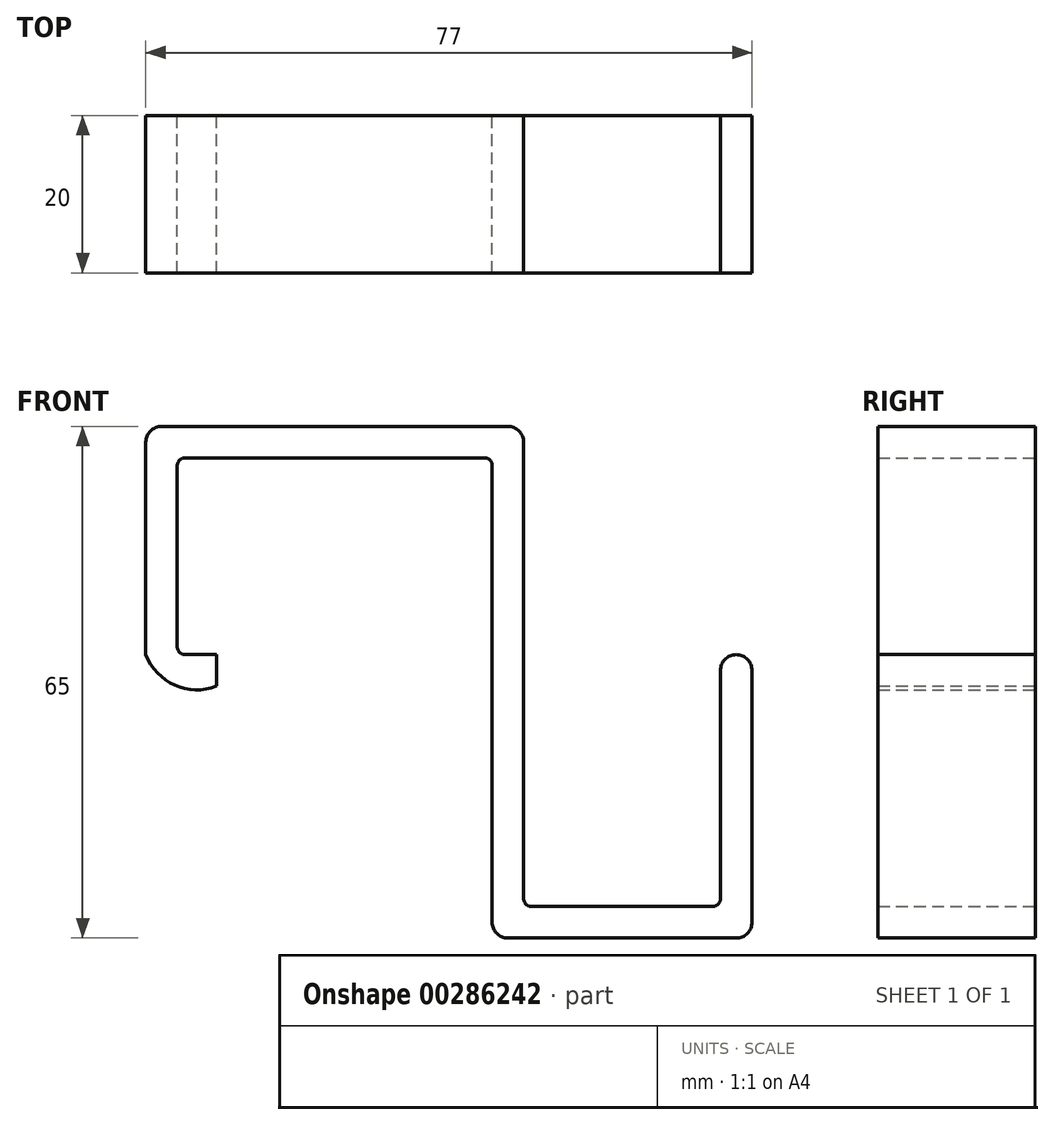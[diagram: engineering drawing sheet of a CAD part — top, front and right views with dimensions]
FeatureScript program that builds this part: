
annotation { "Feature Type Name" : "Feature", "Feature Type Description" : "" }
export const myFeature = defineFeature(function(context is Context, id is Id, definition is map)
    precondition{}
    {
        {
            var Q0;
            Q0=qCreatedBy(makeId("Front.planeOp"),FACE);
            var sketch = newSketch(context, id + "F0", { "sketchPlane" : qUnion([Q0])});
            skLineSegment(sketch, "E0", {"start": v(-24, 0) * mm, "end": v(-24, 29) * mm});
            skLineSegment(sketch, "E1", {"start": v(-24, 29) * mm, "end": v(24, 29) * mm});
            skLineSegment(sketch, "E2", {"start": v(24, 29) * mm, "end": v(24, -32) * mm});
            skLineSegment(sketch, "E3", {"start": v(24, -32) * mm, "end": v(49, -32) * mm});
            skLineSegment(sketch, "E4", {"start": v(49, -32) * mm, "end": v(49, 0) * mm});
            skLineSegment(sketch, "E5", {"start": v(49, 0) * mm, "end": v(53, 0) * mm});
            skLineSegment(sketch, "E6", {"start": v(53, 0) * mm, "end": v(53, -36) * mm});
            skLineSegment(sketch, "E7", {"start": v(53, -36) * mm, "end": v(20, -36) * mm});
            skLineSegment(sketch, "E8", {"start": v(20, -36) * mm, "end": v(20, 25) * mm});
            skLineSegment(sketch, "E9", {"start": v(20, 25) * mm, "end": v(-20, 25) * mm});
            skLineSegment(sketch, "E10", {"start": v(-20, 25) * mm, "end": v(-20, 0) * mm});
            skLineSegment(sketch, "E11", {"start": v(-20, 0) * mm, "end": v(-24, 0) * mm});
            skLineSegment(sketch, "E12", {"start": v(-15, -4) * mm, "end": v(-15, 0) * mm});
            skLineSegment(sketch, "E13", {"start": v(-15, 0) * mm, "end": v(-20, 0) * mm});
            skArc(sketch, "E14", {"start": v(-24, 0) * mm, "mid": v(-20.33, -3.86) * mm, "end": v(-15, -4) * mm});
            skSolve(sketch);
        }
        {
            var Q0;
            Q0 = qSketchRegion(id + "F0", true);
            extrude(context, id + "F1", {"entities" : qUnion([Q0]), "depth" : 20 * mm});
        }
        {
            var Q0;
            Q0=makeQuery(id+"F1.opExtrude","SWEPT_EDGE",EDGE,{"disambiguationData":[OSD([sQuery(id+"F0.wireOp",EDGE,"E10"),sQuery(id+"F0.wireOp",EDGE,"E11"),sQuery(id+"F0.wireOp",EDGE,"E13")])]});
            var Q1;
            Q1=makeQuery(id+"F1.opExtrude","SWEPT_EDGE",EDGE,{"disambiguationData":[OSD([sQuery(id+"F0.wireOp",EDGE,"E9"),sQuery(id+"F0.wireOp",EDGE,"E10")])]});
            var Q2;
            Q2=makeQuery(id+"F1.opExtrude","SWEPT_EDGE",EDGE,{"disambiguationData":[OSD([sQuery(id+"F0.wireOp",EDGE,"E8"),sQuery(id+"F0.wireOp",EDGE,"E9")])]});
            var Q3;
            Q3=makeQuery(id+"F1.opExtrude","SWEPT_EDGE",EDGE,{"disambiguationData":[OSD([sQuery(id+"F0.wireOp",EDGE,"E2"),sQuery(id+"F0.wireOp",EDGE,"E3")])]});
            var Q4;
            Q4=makeQuery(id+"F1.opExtrude","SWEPT_EDGE",EDGE,{"disambiguationData":[OSD([sQuery(id+"F0.wireOp",EDGE,"E3"),sQuery(id+"F0.wireOp",EDGE,"E4")])]});
            fillet(context, id + "F2", {"entities" : qUnion([Q0, Q1, Q2, Q3, Q4]), "radius" : 1 * mm, "tangentPropagation" : true, "allowEdgeOverflow" : false});
        }
        {
            var Q0;
            Q0=makeQuery(id+"F1.opExtrude","SWEPT_EDGE",EDGE,{"disambiguationData":[OSD([sQuery(id+"F0.wireOp",EDGE,"E0"),sQuery(id+"F0.wireOp",EDGE,"E1")])]});
            var Q1;
            Q1=makeQuery(id+"F1.opExtrude","SWEPT_EDGE",EDGE,{"disambiguationData":[OSD([sQuery(id+"F0.wireOp",EDGE,"E1"),sQuery(id+"F0.wireOp",EDGE,"E2")])]});
            var Q2;
            Q2=makeQuery(id+"F1.opExtrude","SWEPT_EDGE",EDGE,{"disambiguationData":[OSD([sQuery(id+"F0.wireOp",EDGE,"E7"),sQuery(id+"F0.wireOp",EDGE,"E8")])]});
            var Q3;
            Q3=makeQuery(id+"F1.opExtrude","SWEPT_EDGE",EDGE,{"disambiguationData":[OSD([sQuery(id+"F0.wireOp",EDGE,"E6"),sQuery(id+"F0.wireOp",EDGE,"E7")])]});
            var Q4;
            Q4=makeQuery(id+"F1.opExtrude","SWEPT_EDGE",EDGE,{"disambiguationData":[OSD([sQuery(id+"F0.wireOp",EDGE,"E4"),sQuery(id+"F0.wireOp",EDGE,"E5")])]});
            var Q5;
            Q5=makeQuery(id+"F1.opExtrude","SWEPT_EDGE",EDGE,{"disambiguationData":[OSD([sQuery(id+"F0.wireOp",EDGE,"E5"),sQuery(id+"F0.wireOp",EDGE,"E6")])]});
            fillet(context, id + "F3", {"entities" : qUnion([Q0, Q1, Q2, Q3, Q4, Q5]), "radius" : 2 * mm, "tangentPropagation" : true, "allowEdgeOverflow" : false});
        }
    });
